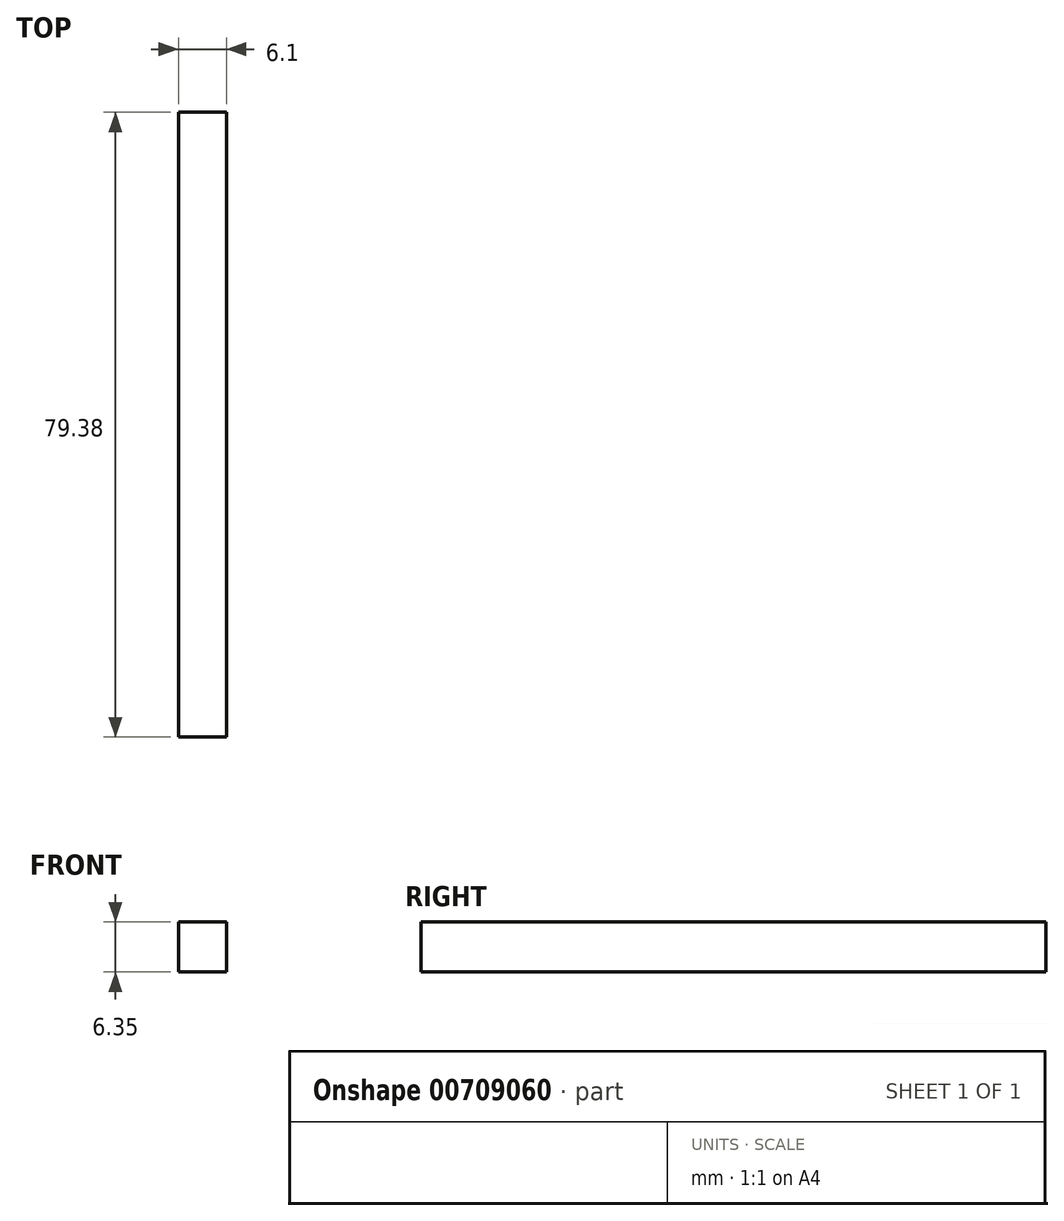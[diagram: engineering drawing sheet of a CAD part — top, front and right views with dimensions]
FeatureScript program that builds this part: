
annotation { "Feature Type Name" : "Feature", "Feature Type Description" : "" }
export const myFeature = defineFeature(function(context is Context, id is Id, definition is map)
    precondition{}
    {
        {
            var Q0;
            Q0=qCreatedBy(makeId("Top.planeOp"),FACE);
            var sketch = newSketch(context, id + "F0", { "sketchPlane" : qUnion([Q0])});
            skLineSegment(sketch, "E0.bottom", {"start": v(0, 0) * mm, "end": v(6.1, 0) * mm});
            skLineSegment(sketch, "E0.top", {"start": v(0, -79.38) * mm, "end": v(6.1, -79.38) * mm});
            skLineSegment(sketch, "E0.left", {"start": v(0, 0) * mm, "end": v(0, -79.38) * mm});
            skLineSegment(sketch, "E0.right", {"start": v(6.1, 0) * mm, "end": v(6.1, -79.38) * mm});
            skSolve(sketch);
        }
        {
            var Q0;
            Q0=makeQuery(id+"F0.imprint","IMPRINT",FACE,{"disambiguationData":[TD([[makeQuery(id+"F0.imprint","IMPRINT",EDGE,{"derivedFrom":sQuery(id+"F0.wireOp",EDGE,"E0.bottom")}),-1.0]])]});
            extrude(context, id + "F1", {"entities" : qUnion([Q0]), "depth" : 6.35 * mm, "offsetDistance" : 25.4 * mm});
        }
    });
